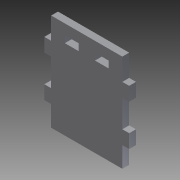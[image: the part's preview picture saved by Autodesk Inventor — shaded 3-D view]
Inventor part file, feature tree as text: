
AUTODESK INVENTOR PART (.ipt)
format: ipt  version: 2011 (Build 150239000, 239)  size: 114,688 bytes
history: native  units: in
note: dims shown in document units (in); Inventor stores cm internally (conversion verified against a paired STEP export)
features: extrude x2, sketch x2
ambient origin geometry x8: Origin, YZ Plane, XZ Plane, XY Plane, X Axis, Y Axis, Z Axis, Center Point
bodies: Solid1 (feature_tree)
feature tree (4):
  extrude  "Extrusion1"  Depth=3.55in
  extrude  "Extrusion2"  Depth=0.75in
  sketch  "Sketch1"  dims[d0=2.6in d1=3.55in]
  sketch  "Sketch2"  dims[d2=3.55in d3=0.75in d4=0.25in d5=0.5in d6=1.0in d7=0.25in d8=0.5in d9=0.75in d10=0.25in d11=0.5in d12=1.0in d13=0.5in d14=0.25in d15=0.0in d16=0.5in d17=0.375in d18=0.5in d19=0.25in d20=0.5in d21=0.5in d22=1.0in d23=0.0in]
